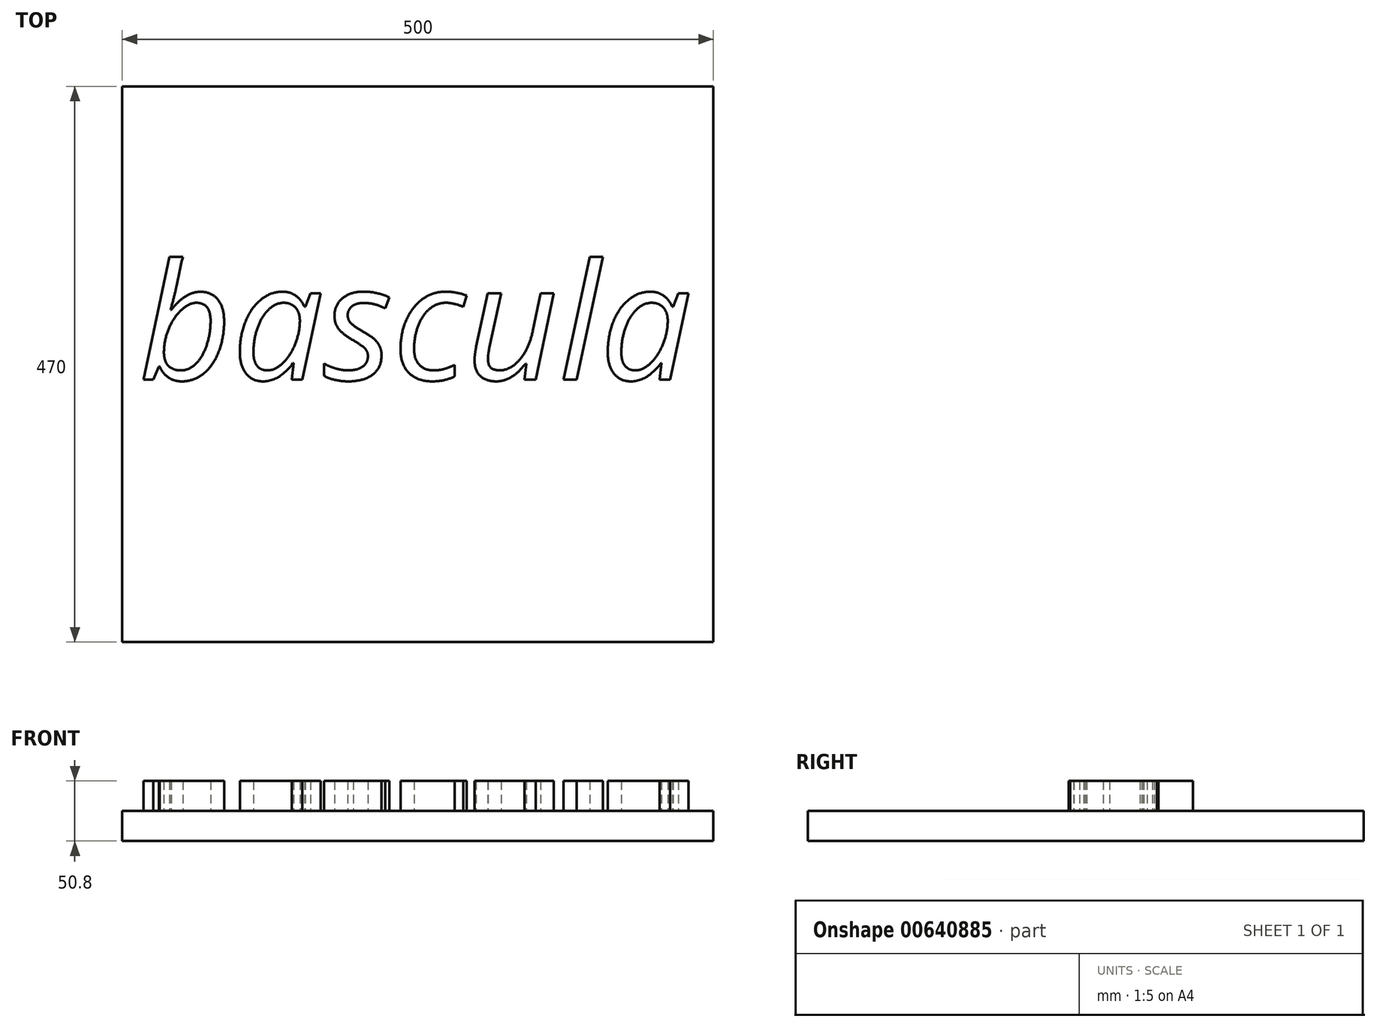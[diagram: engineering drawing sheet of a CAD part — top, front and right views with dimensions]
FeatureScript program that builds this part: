
annotation { "Feature Type Name" : "Feature", "Feature Type Description" : "" }
export const myFeature = defineFeature(function(context is Context, id is Id, definition is map)
    precondition{}
    {
        {
            var Q0;
            Q0=qCreatedBy(makeId("Top.planeOp"),FACE);
            var sketch = newSketch(context, id + "F0", { "sketchPlane" : qUnion([Q0])});
            skLineSegment(sketch, "E0.bottom", {"start": v(-250.86, 386) * mm, "end": v(249.14, 386) * mm});
            skLineSegment(sketch, "E0.top", {"start": v(-250.86, -84) * mm, "end": v(249.14, -84) * mm});
            skLineSegment(sketch, "E0.left", {"start": v(-250.86, 386) * mm, "end": v(-250.86, -84) * mm});
            skLineSegment(sketch, "E0.right", {"start": v(249.14, 386) * mm, "end": v(249.14, -84) * mm});
            skSolve(sketch);
        }
        {
            var Q0;
            Q0 = qSketchRegion(id + "F0", true);
            extrude(context, id + "F1", {"entities" : qUnion([Q0]), "depth" : 25.4 * mm, "offsetDistance" : 25.4 * mm});
        }
        {
            var Q0;
            Q0=makeQuery(id+"F1.opExtrude","CAP_FACE",FACE,{"disambiguationData":[OSD([sQuery(id+"F0.wireOp",EDGE,"E0.bottom"),sQuery(id+"F0.wireOp",EDGE,"E0.top"),sQuery(id+"F0.wireOp",EDGE,"E0.left"),sQuery(id+"F0.wireOp",EDGE,"E0.right")])],"isStart":false});
            var sketch = newSketch(context, id + "F2", { "sketchPlane" : qUnion([Q0])});
            skText(sketch, "E1", { "text": "bascula\n", "fontName": "OpenSans-Italic.ttf"});
            const initialGuessF2  = {"E1": [-0.23694, 0.13787, 1, 0, 0.09851]};
            skSetInitialGuess(sketch, initialGuessF2);
            skSolve(sketch);
        }
        {
            var Q0;
            Q0 = qSketchRegion(id + "F2", true);
            extrude(context, id + "F3", {"entities" : qUnion([Q0]), "operationType" : NewBodyOperationType.ADD, "depth" : 25.4 * mm, "offsetDistance" : 25.4 * mm});
        }
    });
